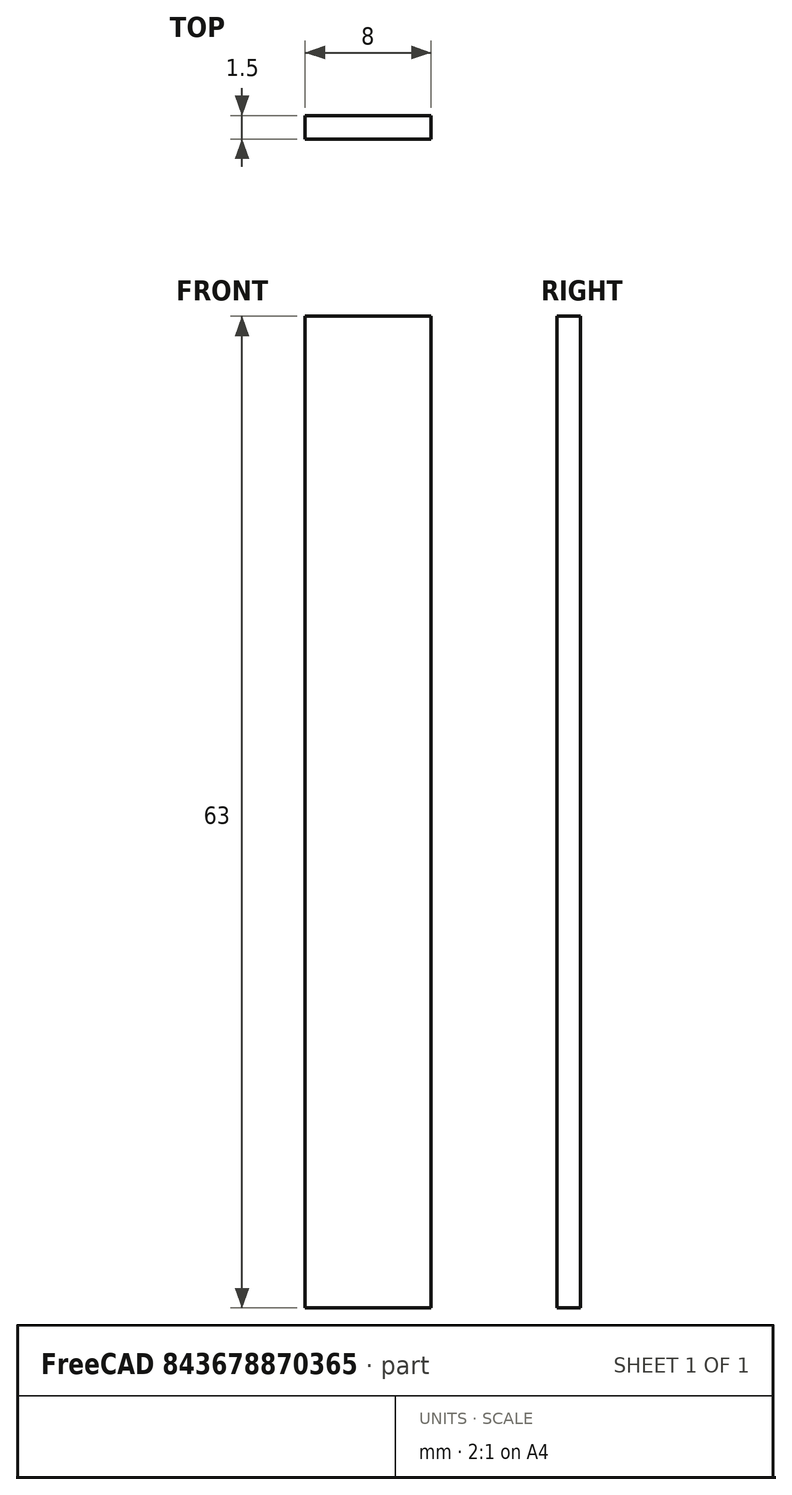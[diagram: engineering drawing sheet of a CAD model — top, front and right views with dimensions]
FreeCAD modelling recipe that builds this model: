
FCSTD DOCUMENT  (FreeCAD 0.14R3700 (Git))
Label: BR_PCB_lateral
License: CC-BY 3.0
LicenseURL: http://creativecommons.org/licenses/by/3.0/
objects: Sketcher::SketchObject×1, Part::Extrusion×1, Part::Feature×1
note: 3 computed .brp shape members not serialized (recipe doc carries the construction recipe); baked Part::Feature solids carry a one-line shape summary decoded from their .brp

FEATURE [Sketcher::SketchObject] Sketch  label="PCB_lateral"
  Placement = pos=(0,0,0) rot=(1,0,0;1.5708rad)
  sketch-geometry (4):
    g0: LineSegment StartX=-4 StartY=31.5 StartZ=0 EndX=4 EndY=31.5 EndZ=0
    g1: LineSegment StartX=4 StartY=31.5 StartZ=0 EndX=4 EndY=-31.5 EndZ=0
    g2: LineSegment StartX=4 StartY=-31.5 StartZ=0 EndX=-4 EndY=-31.5 EndZ=0
    g3: LineSegment StartX=-4 StartY=-31.5 StartZ=0 EndX=-4 EndY=31.5 EndZ=0
  constraints (12):
    c: Coincident(g0,g1)
    c: Coincident(g1,g2)
    c: Coincident(g2,g3)
    c: Coincident(g3,g0)
    c: Horizontal(g0)
    c: Horizontal(g2)
    c: Vertical(g1)
    c: Vertical(g3)
    c: Symmetric(g2,g0,g-1)
    c: Symmetric(g2,g1,g-2)
    c: DistanceY(g3) = 63
    c: DistanceX(g2) = -8
FEATURE [Part::Extrusion] Extrude
  Base = -> Sketch
  Dir = (0,1.5,0)
  Solid = true
FEATURE [Part::Feature] Extrude001  label="PCB_Lateral"
  shape: bbox 8 x 1.5 x 63 mm, 6 faces (baked)
